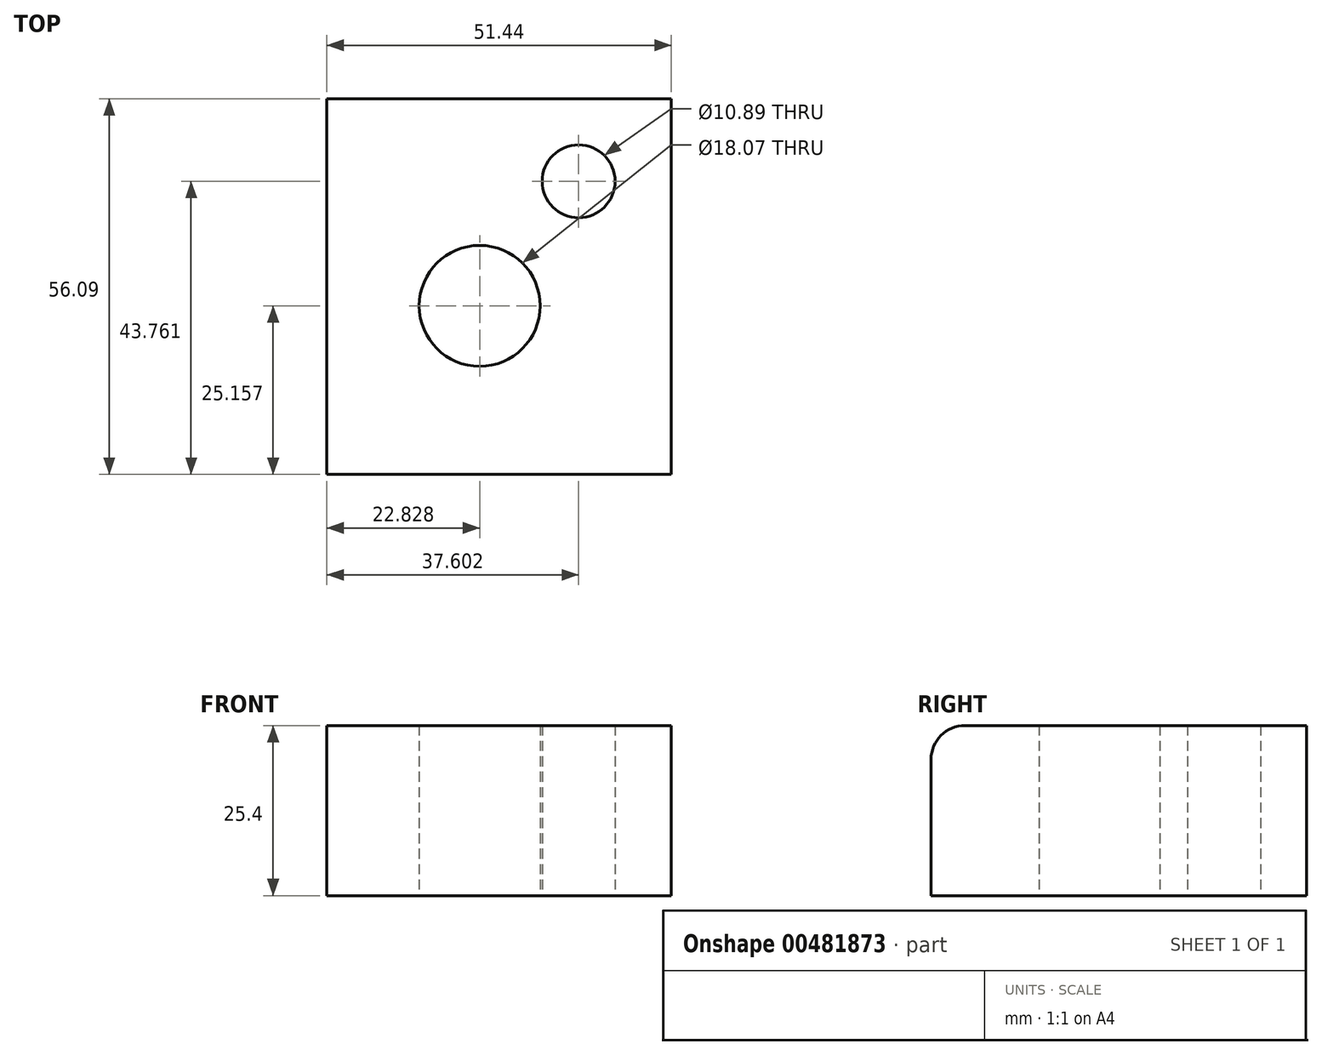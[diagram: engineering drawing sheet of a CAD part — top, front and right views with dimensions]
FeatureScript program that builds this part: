
annotation { "Feature Type Name" : "Feature", "Feature Type Description" : "" }
export const myFeature = defineFeature(function(context is Context, id is Id, definition is map)
    precondition{}
    {
        {
            var Q0;
            Q0=qCreatedBy(makeId("Top.planeOp"),FACE);
            var sketch = newSketch(context, id + "F0", { "sketchPlane" : qUnion([Q0])});
            skLineSegment(sketch, "E0.bottom", {"start": v(0, 0) * mm, "end": v(51.44, 0) * mm});
            skLineSegment(sketch, "E0.top", {"start": v(0, -56.09) * mm, "end": v(51.44, -56.09) * mm});
            skLineSegment(sketch, "E0.left", {"start": v(0, 0) * mm, "end": v(0, -56.09) * mm});
            skLineSegment(sketch, "E0.right", {"start": v(51.44, 0) * mm, "end": v(51.44, -56.09) * mm});
            skCircle(sketch, "E1", {"center": v(37.6, -12.33) * mm, "radius": 5.44 * mm});
            skCircle(sketch, "E2", {"center": v(22.83, -30.93) * mm, "radius": 9.03 * mm});
            skSolve(sketch);
        }
        {
            var Q0;
            Q0 = qSketchRegion(id + "F0", true);
            extrude(context, id + "F1", {"entities" : qUnion([Q0]), "depth" : 25.4 * mm});
        }
        {
            var Q0;
            Q0=makeQuery(id+"F1.opExtrude","CAP_EDGE",EDGE,{"disambiguationData":[OSD([sQuery(id+"F0.wireOp",EDGE,"E0.top")])],"isStart":false});
            fillet(context, id + "F2", {"entities" : qUnion([Q0]), "radius" : 5.08 * mm, "tangentPropagation" : true, "allowEdgeOverflow" : false});
        }
    });
